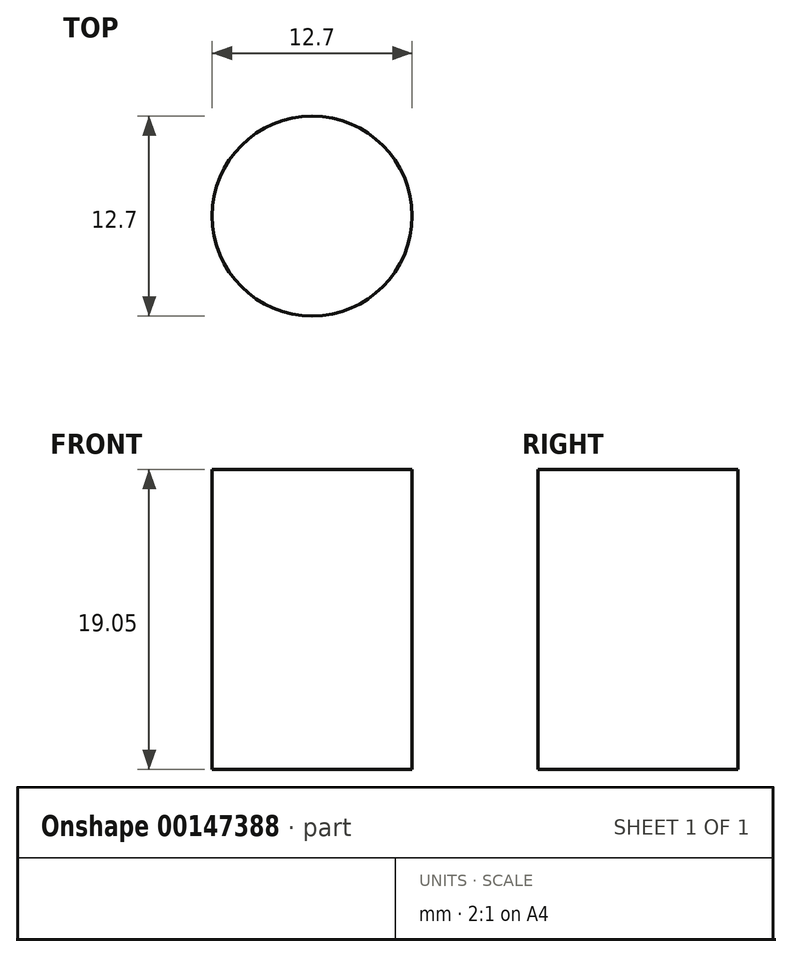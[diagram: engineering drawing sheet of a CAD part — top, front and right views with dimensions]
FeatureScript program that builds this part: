
annotation { "Feature Type Name" : "Feature", "Feature Type Description" : "" }
export const myFeature = defineFeature(function(context is Context, id is Id, definition is map)
    precondition{}
    {
        {
            var Q0;
            Q0=qCreatedBy(makeId("Top.planeOp"),FACE);
            var sketch = newSketch(context, id + "F0", { "sketchPlane" : qUnion([Q0])});
            skCircle(sketch, "E0", {"center": v(0, 0) * mm, "radius": 6.35 * mm});
            skSolve(sketch);
        }
        {
            var Q0;
            Q0 = qSketchRegion(id + "F0", true);
            extrude(context, id + "F1", {"entities" : qUnion([Q0]), "depth" : 19.05 * mm});
        }
    });
